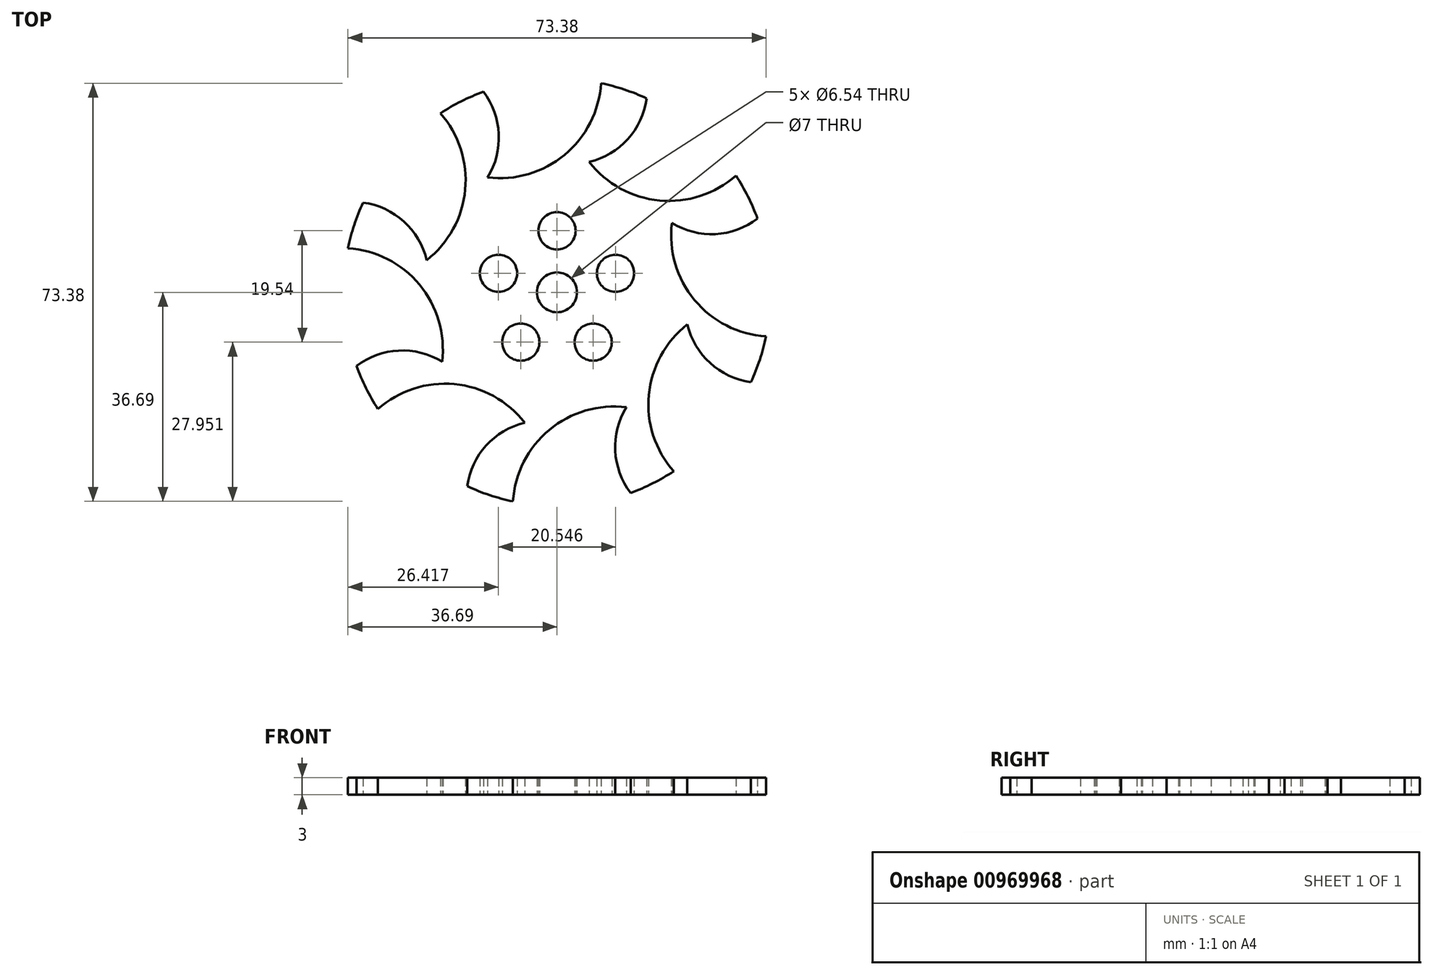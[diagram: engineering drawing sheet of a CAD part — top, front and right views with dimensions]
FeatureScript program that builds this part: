
annotation { "Feature Type Name" : "Feature", "Feature Type Description" : "" }
export const myFeature = defineFeature(function(context is Context, id is Id, definition is map)
    precondition{}
    {
        {
            var Q0;
            Q0=qCreatedBy(makeId("Top.planeOp"),FACE);
            var sketch = newSketch(context, id + "F0", { "sketchPlane" : qUnion([Q0])});
            skLineSegment(sketch, "E0.bottom", {"start": v(-37.5, 37.17) * mm, "end": v(37.5, 37.17) * mm});
            skLineSegment(sketch, "E0.top", {"start": v(-37.5, -37.83) * mm, "end": v(37.5, -37.83) * mm});
            skLineSegment(sketch, "E0.left", {"start": v(-37.5, 37.17) * mm, "end": v(-37.5, -37.83) * mm});
            skLineSegment(sketch, "E0.right", {"start": v(37.5, 37.17) * mm, "end": v(37.5, -37.83) * mm});
            skPoint(sketch, "E0.middle", {"position": v(0, -0.33) * mm});
            skCircle(sketch, "E1", {"center": v(0, 0) * mm, "radius": 3.5 * mm});
            skCircle(sketch, "E2", {"center": v(0, 0) * mm, "radius": 37.5 * mm});
            skLineSegment(sketch, "E3", {"start": v(21.6, 10.45) * mm, "end": v(22.42, 11.07) * mm});
            skPoint(sketch, "E4.end.orphan", {"position": v(20.05, 31.69) * mm});
            skPoint(sketch, "E5.start.orphan", {"position": v(20.05, 25.6) * mm});
            skPoint(sketch, "E6.end.orphan", {"position": v(22.75, 25.6) * mm});
            skPoint(sketch, "E7.end.orphan", {"position": v(20.05, 18.27) * mm});
            skPoint(sketch, "E8.start.orphan", {"position": v(20.05, 13.64) * mm});
            skPoint(sketch, "E9.endSnap0", {"position": v(21.6, 10.45) * mm});
            skArc(sketch, "E10", {"start": v(-12.19, 20.17) * mm, "mid": v(-10.22, 27.8) * mm, "end": v(-12.93, 35.2) * mm});
            skArc(sketch, "E11", {"start": v(-12.19, 20.17) * mm, "mid": v(1.34, 24.13) * mm, "end": v(7.73, 36.7) * mm});
            skArc(sketch, "E12.1.0", {"start": v(-22.88, 5.64) * mm, "mid": v(-26.89, 12.43) * mm, "end": v(-34.03, 15.75) * mm});
            skArc(sketch, "E12.1.1", {"start": v(-22.88, 5.64) * mm, "mid": v(-16.12, 18.01) * mm, "end": v(-20.48, 31.42) * mm});
            skArc(sketch, "E12.2.0", {"start": v(-20.17, -12.19) * mm, "mid": v(-27.8, -10.22) * mm, "end": v(-35.2, -12.93) * mm});
            skArc(sketch, "E12.2.1", {"start": v(-20.17, -12.19) * mm, "mid": v(-24.13, 1.34) * mm, "end": v(-36.7, 7.73) * mm});
            skArc(sketch, "E12.3.0", {"start": v(-5.64, -22.88) * mm, "mid": v(-12.43, -26.89) * mm, "end": v(-15.75, -34.03) * mm});
            skArc(sketch, "E12.3.1", {"start": v(-5.64, -22.88) * mm, "mid": v(-18.01, -16.12) * mm, "end": v(-31.42, -20.48) * mm});
            skArc(sketch, "E12.4.0", {"start": v(12.19, -20.17) * mm, "mid": v(10.22, -27.8) * mm, "end": v(12.93, -35.2) * mm});
            skArc(sketch, "E12.4.1", {"start": v(12.19, -20.17) * mm, "mid": v(-1.34, -24.13) * mm, "end": v(-7.73, -36.7) * mm});
            skArc(sketch, "E12.5.0", {"start": v(22.88, -5.64) * mm, "mid": v(26.89, -12.43) * mm, "end": v(34.03, -15.75) * mm});
            skArc(sketch, "E12.5.1", {"start": v(22.88, -5.64) * mm, "mid": v(16.12, -18.01) * mm, "end": v(20.48, -31.42) * mm});
            skArc(sketch, "E12.6.0", {"start": v(20.17, 12.19) * mm, "mid": v(27.8, 10.22) * mm, "end": v(35.2, 12.93) * mm});
            skArc(sketch, "E12.6.1", {"start": v(20.17, 12.19) * mm, "mid": v(24.13, -1.34) * mm, "end": v(36.7, -7.73) * mm});
            skArc(sketch, "E12.7.0", {"start": v(5.64, 22.88) * mm, "mid": v(12.43, 26.89) * mm, "end": v(15.75, 34.03) * mm});
            skArc(sketch, "E12.7.1", {"start": v(5.64, 22.88) * mm, "mid": v(18.01, 16.12) * mm, "end": v(31.42, 20.48) * mm});
            skPoint(sketch, "E13.orphan", {"position": v(17.35, 7.27) * mm});
            skPoint(sketch, "E14.orphan", {"position": v(25.84, 13.64) * mm});
            skCircle(sketch, "E15", {"center": v(0, 10.8) * mm, "radius": 3.27 * mm});
            skCircle(sketch, "E16.1.0", {"center": v(-10.27, 3.34) * mm, "radius": 3.27 * mm});
            skCircle(sketch, "E16.2.0", {"center": v(-6.35, -8.74) * mm, "radius": 3.27 * mm});
            skCircle(sketch, "E16.3.0", {"center": v(6.35, -8.74) * mm, "radius": 3.27 * mm});
            skCircle(sketch, "E16.4.0", {"center": v(10.27, 3.34) * mm, "radius": 3.27 * mm});
            skSolve(sketch);
        }
        {
            var Q0;
            {var subQ6=sQuery(id+"F0.wireOp",EDGE,"E9");Q0=makeQuery(id+"F0.imprint","IMPRINT",FACE,{"disambiguationData":[TD([[makeQuery(id+"F0.imprint","IMPRINT",EDGE,{"derivedFrom":subQ6}),1.0]])]});}
            var Q1;
            Q1=makeQuery(id+"F0.imprint","IMPRINT",FACE,{"disambiguationData":[TD([[makeQuery(id+"F0.imprint","IMPRINT",EDGE,{"derivedFrom":sQuery(id+"F0.wireOp",EDGE,"E1")}),-1.0]])]});
            extrude(context, id + "F1", {"entities" : qUnion([Q0, Q1]), "depth" : 3 * mm, "offsetDistance" : 25 * mm});
        }
    });
